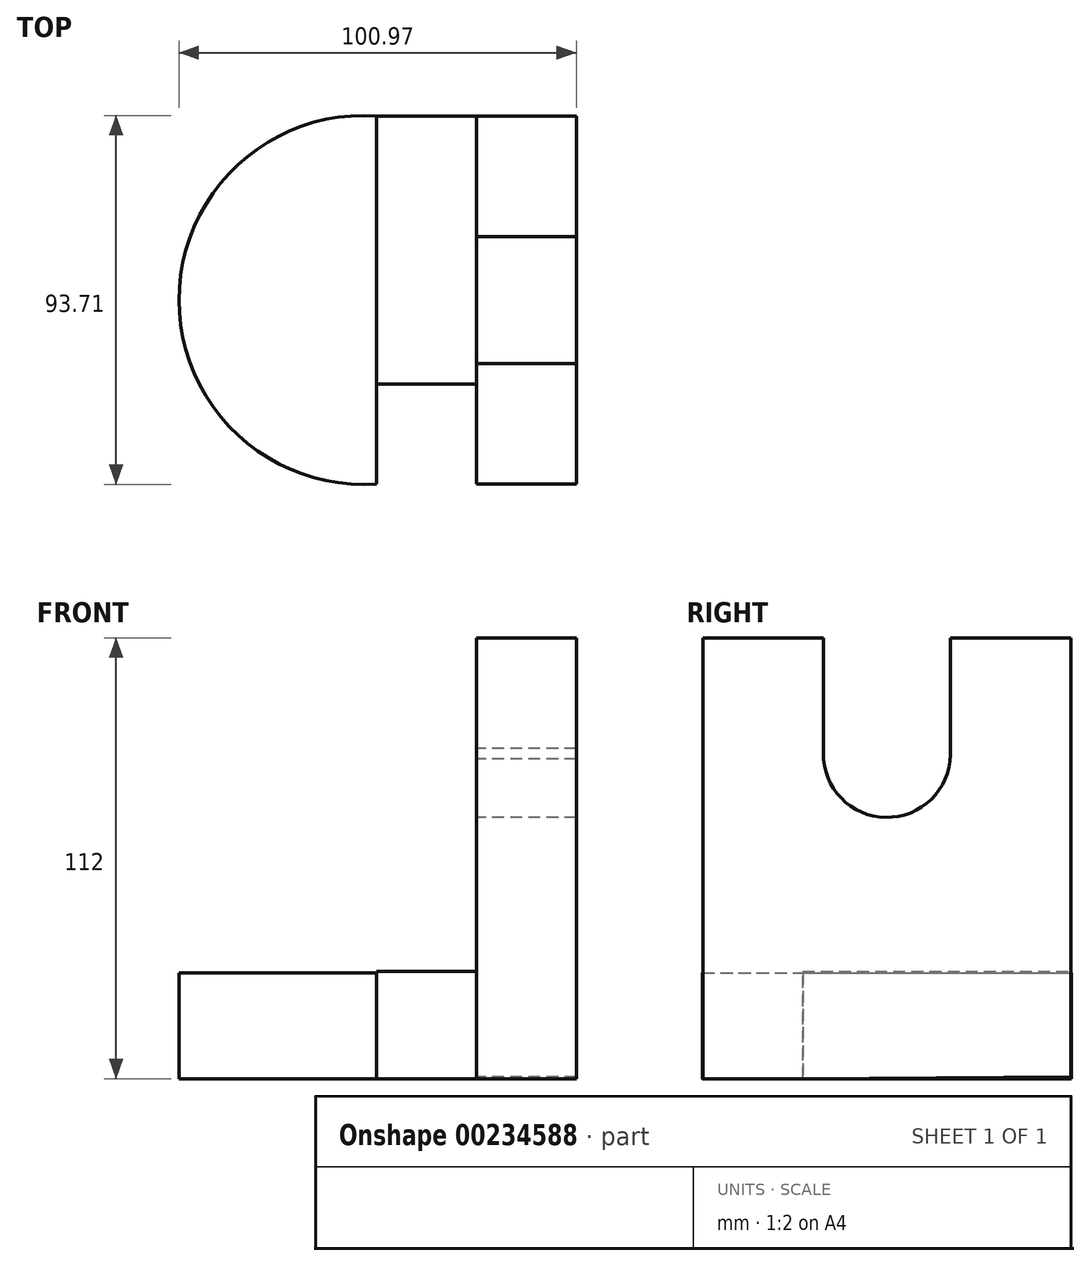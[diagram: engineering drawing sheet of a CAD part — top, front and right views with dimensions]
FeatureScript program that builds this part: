
annotation { "Feature Type Name" : "Feature", "Feature Type Description" : "" }
export const myFeature = defineFeature(function(context is Context, id is Id, definition is map)
    precondition{}
    {
        {
            var Q0;
            Q0=qCreatedBy(makeId("Right.planeOp"),FACE);
            var sketch = newSketch(context, id + "F0", { "sketchPlane" : qUnion([Q0])});
            skLineSegment(sketch, "E0", {"start": v(58.98, -55.84) * mm, "end": v(58.98, 55.68) * mm});
            skLineSegment(sketch, "E1", {"start": v(58.98, 55.68) * mm, "end": v(28.36, 55.68) * mm});
            skLineSegment(sketch, "E2", {"start": v(28.36, 55.68) * mm, "end": v(28.36, 24.9) * mm});
            skArc(sketch, "E3", {"start": v(-3.87, 24.9) * mm, "mid": v(13.58, 10.12) * mm, "end": v(28.36, 27.57) * mm});
            skPoint(sketch, "E3.second.point", {"position": v(-3.87, 24.9) * mm});
            skPoint(sketch, "E3.third.point", {"position": v(-2.42, 19.42) * mm});
            skLineSegment(sketch, "E4", {"start": v(-3.87, 24.9) * mm, "end": v(-3.87, 55.68) * mm});
            skLineSegment(sketch, "E5", {"start": v(-3.87, 55.68) * mm, "end": v(-34.49, 55.68) * mm});
            skLineSegment(sketch, "E6", {"start": v(-34.49, 55.68) * mm, "end": v(-34.49, -29.09) * mm});
            skLineSegment(sketch, "E7", {"start": v(-34.49, -29.09) * mm, "end": v(-9.35, -29.09) * mm});
            skLineSegment(sketch, "E8", {"start": v(-9.35, -29.09) * mm, "end": v(-9.35, -56.32) * mm});
            skLineSegment(sketch, "E9", {"start": v(-9.35, -56.32) * mm, "end": v(58.98, -55.84) * mm});
            skSolve(sketch);
        }
        {
            var Q0;
            Q0=makeQuery(id+"F0.imprint","IMPRINT",FACE,{"disambiguationData":[TD([[makeQuery(id+"F0.imprint","IMPRINT",EDGE,{"derivedFrom":sQuery(id+"F0.wireOp",EDGE,"E0")}),1.0]])]});
            extrude(context, id + "F1", {"entities" : qUnion([Q0]), "depth" : 25.4 * mm});
        }
        {
            var Q0;
            Q0=makeQuery(id+"F1.opExtrude","CAP_FACE",FACE,{"disambiguationData":[OSD([sQuery(id+"F0.wireOp",EDGE,"E0"),sQuery(id+"F0.wireOp",EDGE,"E1"),sQuery(id+"F0.wireOp",EDGE,"E2"),sQuery(id+"F0.wireOp",EDGE,"E3"),sQuery(id+"F0.wireOp",EDGE,"E4"),sQuery(id+"F0.wireOp",EDGE,"E5"),sQuery(id+"F0.wireOp",EDGE,"E6"),sQuery(id+"F0.wireOp",EDGE,"E7"),sQuery(id+"F0.wireOp",EDGE,"E8"),sQuery(id+"F0.wireOp",EDGE,"E9")])],"isStart":true});
            var sketch = newSketch(context, id + "F2", { "sketchPlane" : qUnion([Q0])});
            skLineSegment(sketch, "E10.bottom", {"start": v(9.35, -56.32) * mm, "end": v(-58.98, -56.32) * mm});
            skLineSegment(sketch, "E10.top", {"start": v(9.35, -29.09) * mm, "end": v(-58.98, -29.09) * mm});
            skLineSegment(sketch, "E10.left", {"start": v(9.35, -56.32) * mm, "end": v(9.35, -29.09) * mm});
            skLineSegment(sketch, "E10.right", {"start": v(-58.98, -56.32) * mm, "end": v(-58.98, -29.09) * mm});
            skSolve(sketch);
        }
        {
            var Q0;
            Q0 = qSketchRegion(id + "F2", true);
            extrude(context, id + "F3", {"entities" : qUnion([Q0]), "operationType" : NewBodyOperationType.ADD, "depth" : 25.4 * mm});
        }
        {
            var Q0;
            Q0=makeQuery(id+"F3.boolean.opBoolean","MERGE",FACE,{"derivedFrom":[makeQuery(id+"F1.opExtrude","SWEPT_FACE",FACE,{"disambiguationData":[OSD([sQuery(id+"F0.wireOp",EDGE,"E8")])]}),makeQuery(id+"F3.opExtrude","SWEPT_FACE",FACE,{"disambiguationData":[OSD([sQuery(id+"F2.wireOp",EDGE,"E10.left")])]})]});
            var sketch = newSketch(context, id + "F4", { "sketchPlane" : qUnion([Q0])});
            skLineSegment(sketch, "E11.bottom", {"start": v(-25.4, -56.32) * mm, "end": v(0, -56.32) * mm});
            skLineSegment(sketch, "E11.top", {"start": v(-25.4, -29.09) * mm, "end": v(0, -29.09) * mm});
            skLineSegment(sketch, "E11.left", {"start": v(-25.4, -56.32) * mm, "end": v(-25.4, -29.09) * mm});
            skLineSegment(sketch, "E11.right", {"start": v(0, -56.32) * mm, "end": v(0, -29.09) * mm});
            skSolve(sketch);
        }
        {
            var Q0;
            Q0=makeQuery(id+"F4.imprint","IMPRINT",FACE,{"disambiguationData":[TD([[makeQuery(id+"F4.imprint","IMPRINT",EDGE,{"derivedFrom":sQuery(id+"F4.wireOp",EDGE,"E11.right")}),-1.0]])]});
            var Q1;
            Q1=makeQuery(id+"F4.imprint","IMPRINT",FACE,{"disambiguationData":[TD([[makeQuery(id+"F4.imprint","IMPRINT",EDGE,{"derivedFrom":sQuery(id+"F4.wireOp",EDGE,"E11.bottom")}),1.0]])]});
            extrude(context, id + "F5", {"entities" : qUnion([Q0, Q1]), "operationType" : NewBodyOperationType.ADD, "depth" : 25.15 * mm});
        }
        {
            var Q0;
            Q0=makeQuery(id+"F5.boolean.opBoolean","MERGE",FACE,{"derivedFrom":[makeQuery(id+"F3.opExtrude","SWEPT_FACE",FACE,{"disambiguationData":[OSD([sQuery(id+"F2.wireOp",EDGE,"E10.bottom")])]}),makeQuery(id+"F5.opExtrude","SWEPT_FACE",FACE,{"disambiguationData":[OSD([sQuery(id+"F0.wireOp",EDGE,"E8"),sQuery(id+"F0.wireOp",EDGE,"E9"),sQuery(id+"F4.wireOp",EDGE,"E11.bottom")])]})]});
            var sketch = newSketch(context, id + "F6", { "sketchPlane" : qUnion([Q0])});
            skArc(sketch, "E12", {"start": v(-25.4, 34.5) * mm, "mid": v(-75.57, -12.24) * mm, "end": v(-25.4, -58.98) * mm});
            skSolve(sketch);
        }
        {
            var Q0;
            Q0 = qSketchRegion(id + "F6", true);
            var Q1;
            Q1=makeQuery(id+"F6.imprint","IMPRINT",FACE,{"disambiguationData":[TD([[makeQuery(id+"F6.imprint","IMPRINT",EDGE,{"derivedFrom":sQuery(id+"F6.wireOp",EDGE,"E12")}),1.0]])]});
            extrude(context, id + "F7", {"entities" : qUnion([Q0, Q1]), "operationType" : NewBodyOperationType.ADD, "oppositeDirection" : true, "depth" : 26.92 * mm});
        }
        {
            var Q0;
            Q0=makeQuery(id+"F5.opExtrude","CAP_FACE",FACE,{"disambiguationData":[OSD([sQuery(id+"F0.wireOp",EDGE,"E7"),sQuery(id+"F0.wireOp",EDGE,"E8"),sQuery(id+"F0.wireOp",EDGE,"E9"),sQuery(id+"F4.wireOp",EDGE,"E11.bottom"),sQuery(id+"F4.wireOp",EDGE,"E11.top"),sQuery(id+"F4.wireOp",EDGE,"E11.left")])],"isStart":false});
            var sketch = newSketch(context, id + "F8", { "sketchPlane" : qUnion([Q0])});
            skLineSegment(sketch, "E13.bottom", {"start": v(-25.4, -56.32) * mm, "end": v(0, -56.32) * mm});
            skLineSegment(sketch, "E13.top", {"start": v(-25.4, -29.09) * mm, "end": v(0, -29.09) * mm});
            skLineSegment(sketch, "E13.left", {"start": v(-25.4, -56.32) * mm, "end": v(-25.4, -29.09) * mm});
            skLineSegment(sketch, "E13.right", {"start": v(0, -56.32) * mm, "end": v(0, -29.09) * mm});
            skSolve(sketch);
        }
        {
            var Q0;
            Q0 = qSketchRegion(id + "F8", true);
            extrude(context, id + "F9", {"entities" : qUnion([Q0]), "operationType" : NewBodyOperationType.REMOVE, "oppositeDirection" : true, "depth" : 25.4 * mm});
        }
    });
